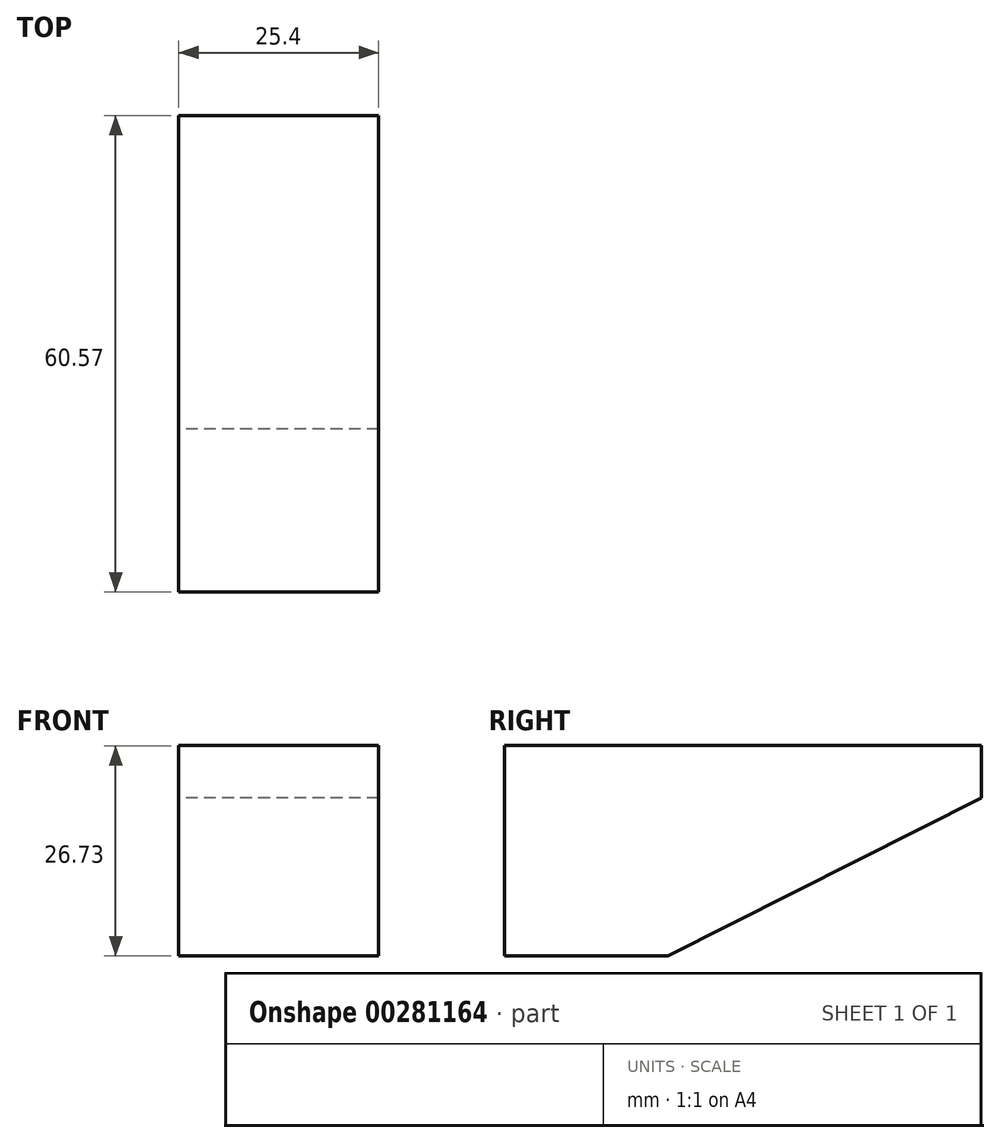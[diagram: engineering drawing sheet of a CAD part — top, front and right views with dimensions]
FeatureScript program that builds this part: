
annotation { "Feature Type Name" : "Feature", "Feature Type Description" : "" }
export const myFeature = defineFeature(function(context is Context, id is Id, definition is map)
    precondition{}
    {
        {
            var Q0;
            Q0=qCreatedBy(makeId("Right.planeOp"),FACE);
            var sketch = newSketch(context, id + "F0", { "sketchPlane" : qUnion([Q0])});
            skLineSegment(sketch, "E0", {"start": v(0, 26.73) * mm, "end": v(39.82, 26.73) * mm});
            skLineSegment(sketch, "E1", {"start": v(39.82, 26.73) * mm, "end": v(39.82, 20.12) * mm});
            skLineSegment(sketch, "E2", {"start": v(0, 0) * mm, "end": v(39.82, 20.12) * mm});
            skLineSegment(sketch, "E3", {"start": v(0, 26.73) * mm, "end": v(-20.75, 26.73) * mm});
            skLineSegment(sketch, "E4", {"start": v(-20.75, 26.73) * mm, "end": v(-20.75, 10.79) * mm});
            skLineSegment(sketch, "E5", {"start": v(-20.75, 10.79) * mm, "end": v(-20.75, 0) * mm});
            skLineSegment(sketch, "E6", {"start": v(-20.75, 0) * mm, "end": v(0, 0) * mm});
            skSolve(sketch);
        }
        {
            var Q0;
            Q0=makeQuery(id+"F0.imprint","IMPRINT",FACE,{"disambiguationData":[TD([[makeQuery(id+"F0.imprint","IMPRINT",EDGE,{"derivedFrom":sQuery(id+"F0.wireOp",EDGE,"E0")}),-1.0]])]});
            extrude(context, id + "F1", {"entities" : qUnion([Q0]), "depth" : 25.4 * mm});
        }
    });
